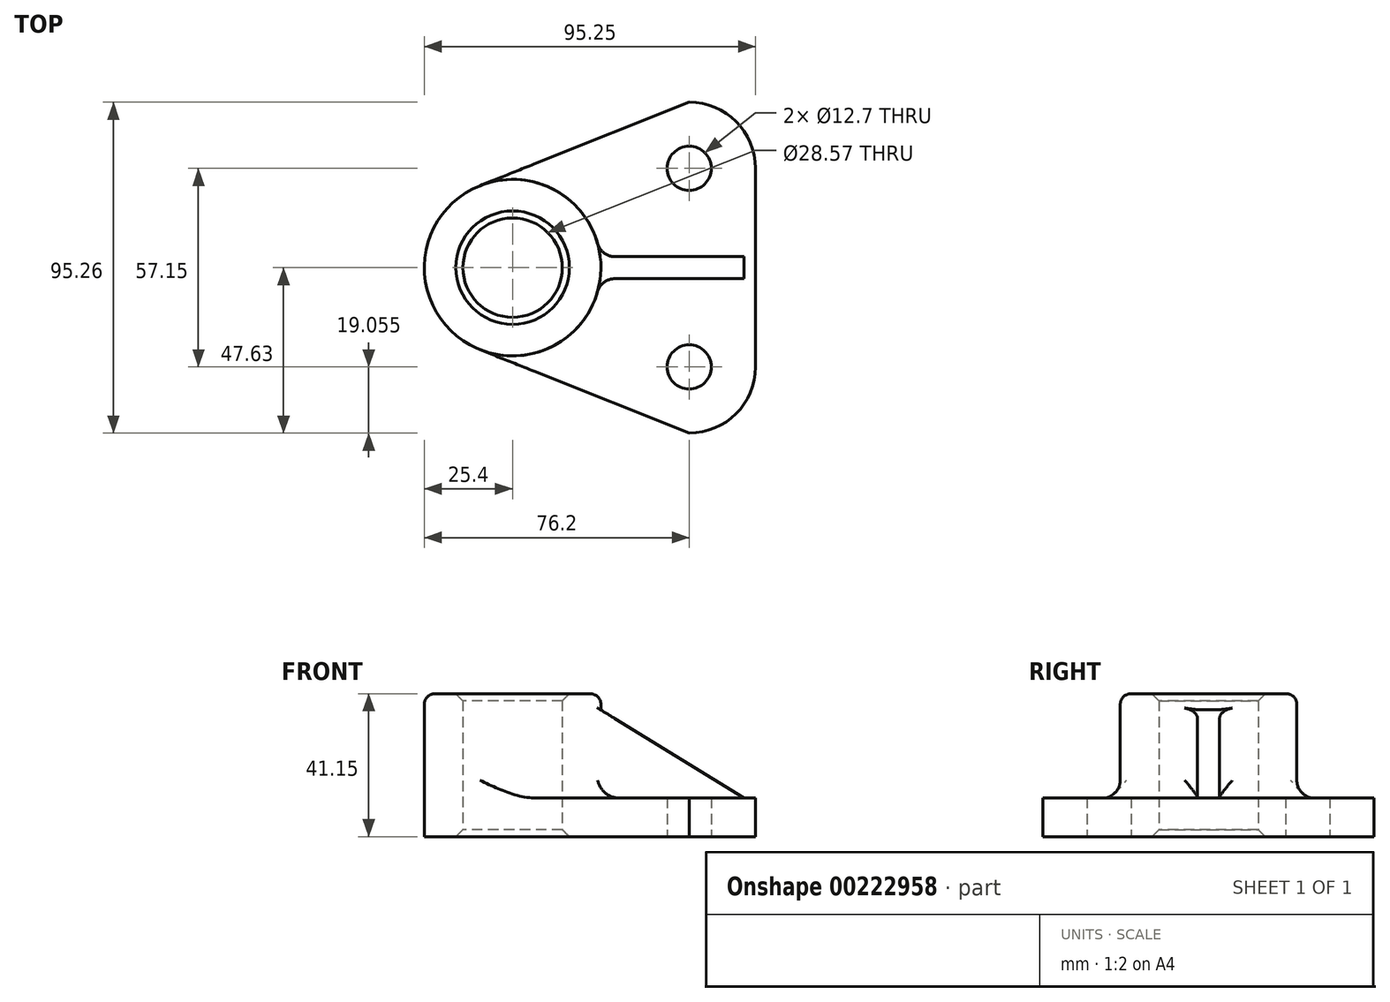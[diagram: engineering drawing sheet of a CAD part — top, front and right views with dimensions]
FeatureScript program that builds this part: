
annotation { "Feature Type Name" : "Feature", "Feature Type Description" : "" }
export const myFeature = defineFeature(function(context is Context, id is Id, definition is map)
    precondition{}
    {
        {
            var Q0;
            Q0=qCreatedBy(makeId("Top.planeOp"),FACE);
            var sketch = newSketch(context, id + "F0", { "sketchPlane" : qUnion([Q0])});
            skCircle(sketch, "E0", {"center": v(25.05, 28.58) * mm, "radius": 6.35 * mm});
            skCircle(sketch, "E1", {"center": v(25.05, -28.57) * mm, "radius": 6.35 * mm});
            skArc(sketch, "E2", {"start": v(44.1, 28.58) * mm, "mid": v(38.52, 42.05) * mm, "end": v(25.05, 47.63) * mm});
            skArc(sketch, "E3", {"start": v(25.05, -47.62) * mm, "mid": v(38.52, -42.05) * mm, "end": v(44.1, -28.57) * mm});
            skLineSegment(sketch, "E4", {"start": v(44.1, -28.57) * mm, "end": v(44.1, 28.58) * mm});
            skCircle(sketch, "E5", {"center": v(-25.75, 0) * mm, "radius": 25.4 * mm});
            skCircle(sketch, "E6", {"center": v(-25.75, 0) * mm, "radius": 14.29 * mm});
            skLineSegment(sketch, "E7", {"start": v(25.05, -47.62) * mm, "end": v(-35.17, -23.6) * mm});
            skLineSegment(sketch, "E8", {"start": v(-35.17, 23.6) * mm, "end": v(25.05, 47.63) * mm});
            skSolve(sketch);
        }
        {
            var Q0;
            Q0=makeQuery(id+"F0.imprint","IMPRINT",FACE,{"disambiguationData":[TD([[makeQuery(id+"F0.imprint","IMPRINT",EDGE,{"derivedFrom":sQuery(id+"F0.wireOp",EDGE,"E6")}),-1.0]])]});
            extrude(context, id + "F1", {"entities" : qUnion([Q0]), "depth" : 41.15 * mm});
        }
        {
            var Q0;
            Q0 = qSketchRegion(id + "F0", true);
            extrude(context, id + "F2", {"entities" : qUnion([Q0]), "operationType" : NewBodyOperationType.ADD, "depth" : 11.18 * mm});
        }
        {
            var Q0;
            Q0=makeQuery(id+"F2.opExtrude","CAP_FACE",FACE,{"disambiguationData":[OSD([sQuery(id+"F0.wireOp",EDGE,"E0"),sQuery(id+"F0.wireOp",EDGE,"E1"),sQuery(id+"F0.wireOp",EDGE,"E2"),sQuery(id+"F0.wireOp",EDGE,"E3"),sQuery(id+"F0.wireOp",EDGE,"E4"),sQuery(id+"F0.wireOp",EDGE,"E5"),sQuery(id+"F0.wireOp",EDGE,"E6"),sQuery(id+"F0.wireOp",EDGE,"E7"),sQuery(id+"F0.wireOp",EDGE,"E8")])],"isStart":false});
            var sketch = newSketch(context, id + "F3", { "sketchPlane" : qUnion([Q0])});
            skLineSegment(sketch, "E9", {"start": v(-0.35, 0) * mm, "end": v(40.8, 0) * mm});
            skLineSegment(sketch, "E10.bottom", {"start": v(40.8, 3.17) * mm, "end": v(-2.92, 3.17) * mm});
            skLineSegment(sketch, "E10.top", {"start": v(40.8, -3.18) * mm, "end": v(-2.92, -3.18) * mm});
            skPoint(sketch, "E10.middle", {"position": v(0, 0) * mm});
            skLineSegment(sketch, "E11", {"start": v(-2.92, -3.18) * mm, "end": v(-2.92, 3.17) * mm});
            skLineSegment(sketch, "E12", {"start": v(40.8, 3.17) * mm, "end": v(40.8, -3.18) * mm});
            skPoint(sketch, "E13.end.orphan", {"position": v(40.8, 0) * mm});
            skSolve(sketch);
        }
        {
            var Q0;
            Q0 = qSketchRegion(id + "F3", true);
            extrude(context, id + "F4", {"entities" : qUnion([Q0]), "operationType" : NewBodyOperationType.ADD, "depth" : 25.4 * mm});
        }
        {
            var Q0;
            Q0=qCreatedBy(makeId("Front.planeOp"),FACE);
            var sketch = newSketch(context, id + "F5", { "sketchPlane" : qUnion([Q0])});
            skLineSegment(sketch, "E14", {"start": v(40.8, 11.18) * mm, "end": v(-0.55, 36.58) * mm});
            skLineSegment(sketch, "E15", {"start": v(-0.55, 36.58) * mm, "end": v(40.8, 36.58) * mm});
            skLineSegment(sketch, "E16", {"start": v(40.8, 36.58) * mm, "end": v(40.8, 11.18) * mm});
            skSolve(sketch);
        }
        {
            var Q0;
            Q0 = qSketchRegion(id + "F5", true);
            extrude(context, id + "F6", {"entities" : qUnion([Q0]), "operationType" : NewBodyOperationType.REMOVE, "endBound" : BoundingType.SYMMETRIC, "oppositeDirection" : true, "depth" : 25.4 * mm});
        }
        {
            var Q0;
            {var subQ0=sQuery(id+"F0.wireOp",EDGE,"E5");var subQ1=makeQuery(id+"F1.opExtrude","SWEPT_FACE",FACE,{"disambiguationData":[OSD([subQ0])]});var subQ2=sQuery(id+"F0.wireOp",EDGE,"E7");var subQ3=makeQuery(id+"F2.opExtrude","CAP_FACE",FACE,{"disambiguationData":[OSD([sQuery(id+"F0.wireOp",EDGE,"E0"),sQuery(id+"F0.wireOp",EDGE,"E1"),sQuery(id+"F0.wireOp",EDGE,"E2"),sQuery(id+"F0.wireOp",EDGE,"E3"),sQuery(id+"F0.wireOp",EDGE,"E4"),subQ0,sQuery(id+"F0.wireOp",EDGE,"E6"),subQ2,sQuery(id+"F0.wireOp",EDGE,"E8")])],"isStart":false});Q0=makeQuery(id+"F4.boolean.opBoolean","SPLIT",EDGE,{"disambiguationData":[TD([makeQuery(id+"F2.opExtrude","SWEPT_FACE",FACE,{"disambiguationData":[OSD([subQ2])]})])],"derivedFrom":makeQuery(id+"F2.boolean.opBoolean","INTERSECT",EDGE,{"derivedFrom":[subQ1,subQ3]})});}
            var Q1;
            Q1=makeQuery(id+"F4.boolean.opBoolean","INTERSECT",EDGE,{"derivedFrom":[makeQuery(id+"F1.opExtrude","SWEPT_FACE",FACE,{"disambiguationData":[OSD([sQuery(id+"F0.wireOp",EDGE,"E5")])]}),makeQuery(id+"F4.opExtrude","SWEPT_FACE",FACE,{"disambiguationData":[OSD([sQuery(id+"F3.wireOp",EDGE,"E10.top")])]})]});
            var Q2;
            Q2=makeQuery(id+"F4.opExtrude","CAP_EDGE",EDGE,{"disambiguationData":[OSD([sQuery(id+"F3.wireOp",EDGE,"E10.top")])],"isStart":true});
            var Q3;
            Q3=makeQuery(id+"F4.boolean.opBoolean","INTERSECT",EDGE,{"derivedFrom":[makeQuery(id+"F1.opExtrude","SWEPT_FACE",FACE,{"disambiguationData":[OSD([sQuery(id+"F0.wireOp",EDGE,"E5")])]}),makeQuery(id+"F4.opExtrude","SWEPT_FACE",FACE,{"disambiguationData":[OSD([sQuery(id+"F3.wireOp",EDGE,"E10.bottom")])]})]});
            var Q4;
            {var subQ0=sQuery(id+"F0.wireOp",EDGE,"E5");var subQ1=makeQuery(id+"F1.opExtrude","SWEPT_FACE",FACE,{"disambiguationData":[OSD([subQ0])]});var subQ2=sQuery(id+"F0.wireOp",EDGE,"E8");var subQ3=makeQuery(id+"F2.opExtrude","CAP_FACE",FACE,{"disambiguationData":[OSD([sQuery(id+"F0.wireOp",EDGE,"E0"),sQuery(id+"F0.wireOp",EDGE,"E1"),sQuery(id+"F0.wireOp",EDGE,"E2"),sQuery(id+"F0.wireOp",EDGE,"E3"),sQuery(id+"F0.wireOp",EDGE,"E4"),subQ0,sQuery(id+"F0.wireOp",EDGE,"E6"),sQuery(id+"F0.wireOp",EDGE,"E7"),subQ2])],"isStart":false});Q4=makeQuery(id+"F4.boolean.opBoolean","SPLIT",EDGE,{"disambiguationData":[TD([makeQuery(id+"F2.opExtrude","SWEPT_FACE",FACE,{"disambiguationData":[OSD([subQ2])]})])],"derivedFrom":makeQuery(id+"F2.boolean.opBoolean","INTERSECT",EDGE,{"derivedFrom":[subQ1,subQ3]})});}
            var Q5;
            Q5=makeQuery(id+"F4.opExtrude","CAP_EDGE",EDGE,{"disambiguationData":[OSD([sQuery(id+"F3.wireOp",EDGE,"E10.bottom")])],"isStart":true});
            fillet(context, id + "F7", {"entities" : qUnion([Q0, Q1, Q2, Q3, Q4, Q5]), "radius" : 5.08 * mm, "tangentPropagation" : true, "allowEdgeOverflow" : false});
        }
        {
            var Q0;
            Q0=makeQuery(id+"F1.opExtrude","CAP_EDGE",EDGE,{"disambiguationData":[OSD([sQuery(id+"F0.wireOp",EDGE,"E5")])],"isStart":false});
            fillet(context, id + "F8", {"entities" : qUnion([Q0]), "radius" : 3.05 * mm, "tangentPropagation" : true, "allowEdgeOverflow" : false});
        }
        {
            var Q0;
            Q0=makeQuery(id+"F1.opExtrude","CAP_EDGE",EDGE,{"disambiguationData":[OSD([sQuery(id+"F0.wireOp",EDGE,"E6")])],"isStart":false});
            chamfer(context, id + "F9", {"entities" : qUnion([Q0]), "chamferType" : ChamferType.OFFSET_ANGLE, "width" : 2.03 * mm, "oppositeDirection" : false, "angle" : 45 * degree, "tangentPropagation" : true});
        }
        {
            var Q0;
            Q0=makeQuery(id+"F1.opExtrude","CAP_EDGE",EDGE,{"disambiguationData":[OSD([sQuery(id+"F0.wireOp",EDGE,"E6")])],"isStart":true});
            chamfer(context, id + "F10", {"entities" : qUnion([Q0]), "chamferType" : ChamferType.OFFSET_ANGLE, "width" : 2.03 * mm, "oppositeDirection" : false, "angle" : 45 * degree, "tangentPropagation" : true});
        }
    });
